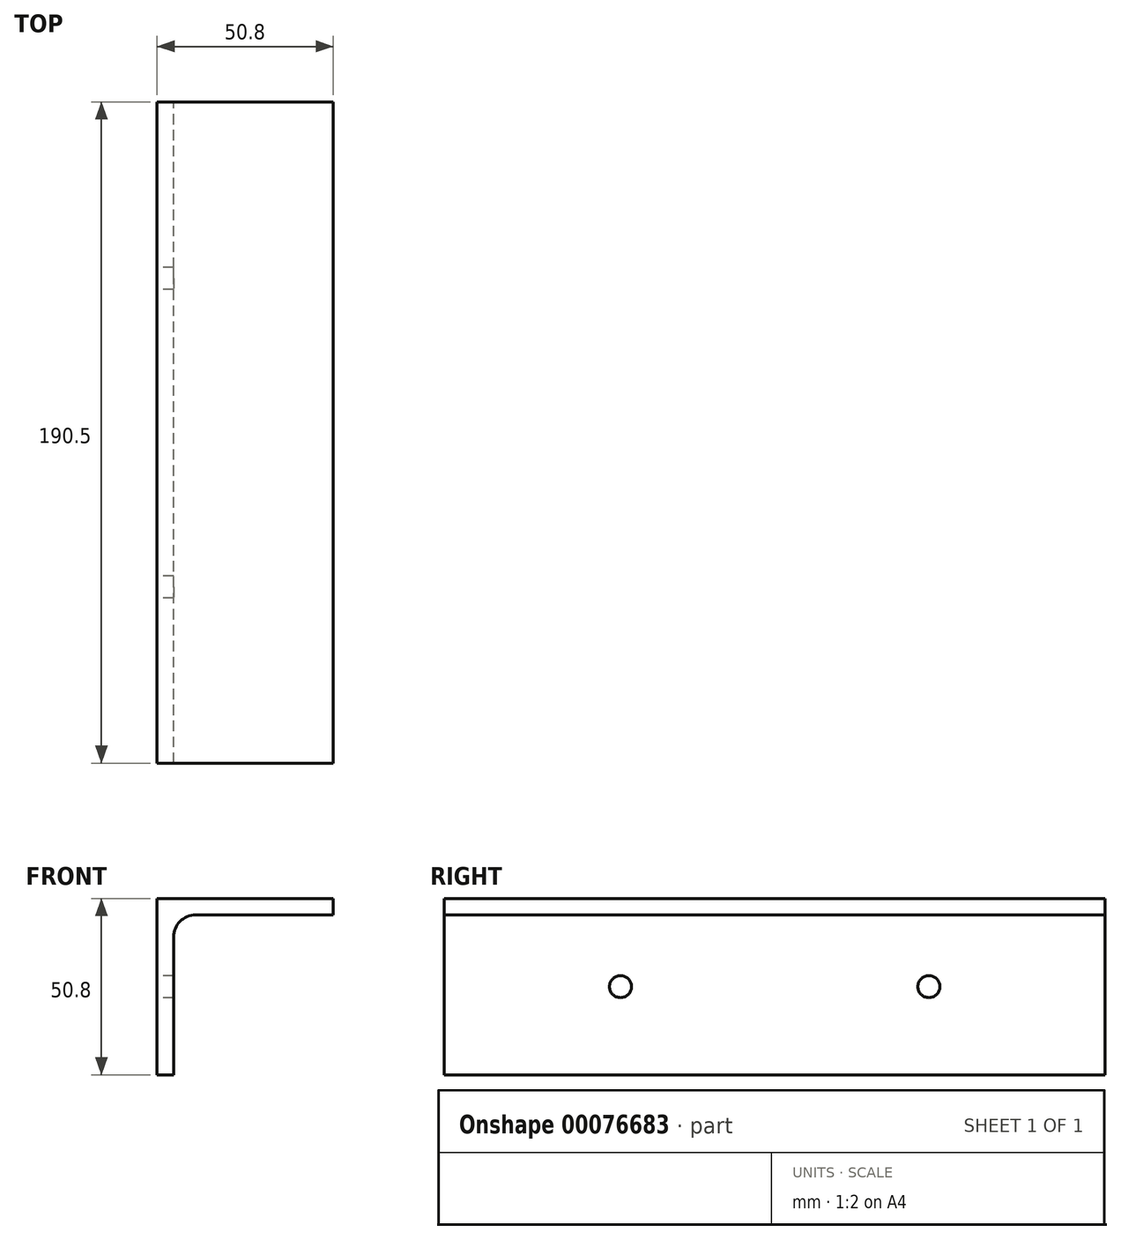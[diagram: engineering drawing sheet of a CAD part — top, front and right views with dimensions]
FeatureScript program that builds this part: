
annotation { "Feature Type Name" : "Feature", "Feature Type Description" : "" }
export const myFeature = defineFeature(function(context is Context, id is Id, definition is map)
    precondition{}
    {
        {
            var Q0;
            Q0=qCreatedBy(makeId("Front.planeOp"),FACE);
            var sketch = newSketch(context, id + "F0", { "sketchPlane" : qUnion([Q0])});
            skLineSegment(sketch, "E0", {"start": v(0, 0) * mm, "end": v(-50.8, 0) * mm});
            skLineSegment(sketch, "E1", {"start": v(-50.8, 0) * mm, "end": v(-50.8, -50.8) * mm});
            skLineSegment(sketch, "E2", {"start": v(-50.8, -50.8) * mm, "end": v(-46.05, -50.8) * mm});
            skLineSegment(sketch, "E3", {"start": v(0, 0) * mm, "end": v(0, -4.75) * mm});
            skLineSegment(sketch, "E4", {"start": v(0, -4.75) * mm, "end": v(-39.7, -4.75) * mm});
            skLineSegment(sketch, "E5", {"start": v(-46.05, -11.1) * mm, "end": v(-46.05, -50.8) * mm});
            skPoint(sketch, "E6.visualSharp", {"position": v(-46.05, -4.75) * mm});
            skArc(sketch, "E6.filletArc", {"start": v(-39.7, -4.75) * mm, "mid": v(-44.2, -6.6) * mm, "end": v(-46.05, -11.1) * mm});
            skSolve(sketch);
        }
        {
            var Q0;
            Q0=makeQuery(id+"F0.imprint","IMPRINT",FACE,{"disambiguationData":[TD([[makeQuery(id+"F0.imprint","IMPRINT",EDGE,{"derivedFrom":sQuery(id+"F0.wireOp",EDGE,"E0")}),1.0]])]});
            extrude(context, id + "F1", {"entities" : qUnion([Q0]), "depth" : 190.5 * mm});
        }
        {
            var Q0;
            Q0=makeQuery(id+"F1.opExtrude","SWEPT_FACE",FACE,{"disambiguationData":[OSD([sQuery(id+"F0.wireOp",EDGE,"E1")])]});
            var sketch = newSketch(context, id + "F2", { "sketchPlane" : qUnion([Q0])});
            skLineSegment(sketch, "E7.0", {"start": v(190.5, -25.4) * mm, "end": v(0, -25.4) * mm, "construction": true});
            skLineSegment(sketch, "E8.0", {"start": v(50.8, 0) * mm, "end": v(50.8, -50.8) * mm, "construction": true});
            skLineSegment(sketch, "E9.0", {"start": v(139.7, 0) * mm, "end": v(139.7, -50.8) * mm, "construction": true});
            skCircle(sketch, "E10", {"center": v(50.8, -25.4) * mm, "radius": 3.18 * mm, "construction": true});
            skCircle(sketch, "E11", {"center": v(139.7, -25.4) * mm, "radius": 3.18 * mm, "construction": true});
            skSolve(sketch);
        }
        {
            var Q0;
            Q0=sQuery(id+"F2.wireOp",VERTEX,"E10.center");
            var Q1;
            Q1=sQuery(id+"F2.wireOp",VERTEX,"E11.center");
            var Q2;
            Q2=makeQuery(id+"F1.opExtrude","SWEPT_BODY",BODY,{"disambiguationData":[OSD([sQuery(id+"F0.wireOp",EDGE,"E0"),sQuery(id+"F0.wireOp",EDGE,"E1"),sQuery(id+"F0.wireOp",EDGE,"E2"),sQuery(id+"F0.wireOp",EDGE,"E3"),sQuery(id+"F0.wireOp",EDGE,"E4"),sQuery(id+"F0.wireOp",EDGE,"E5"),sQuery(id+"F0.wireOp",EDGE,"E6.filletArc")])]});
            hole(context, id + "F3", {"style" : HoleStyle.SIMPLE, "endStyle" : HoleEndStyle.THROUGH, "holeDiameter" : 6.35 * mm, "locations" : qUnion([Q0, Q1]), "scope" : qUnion([Q2]), "isTappedThrough" : true});
        }
    });
